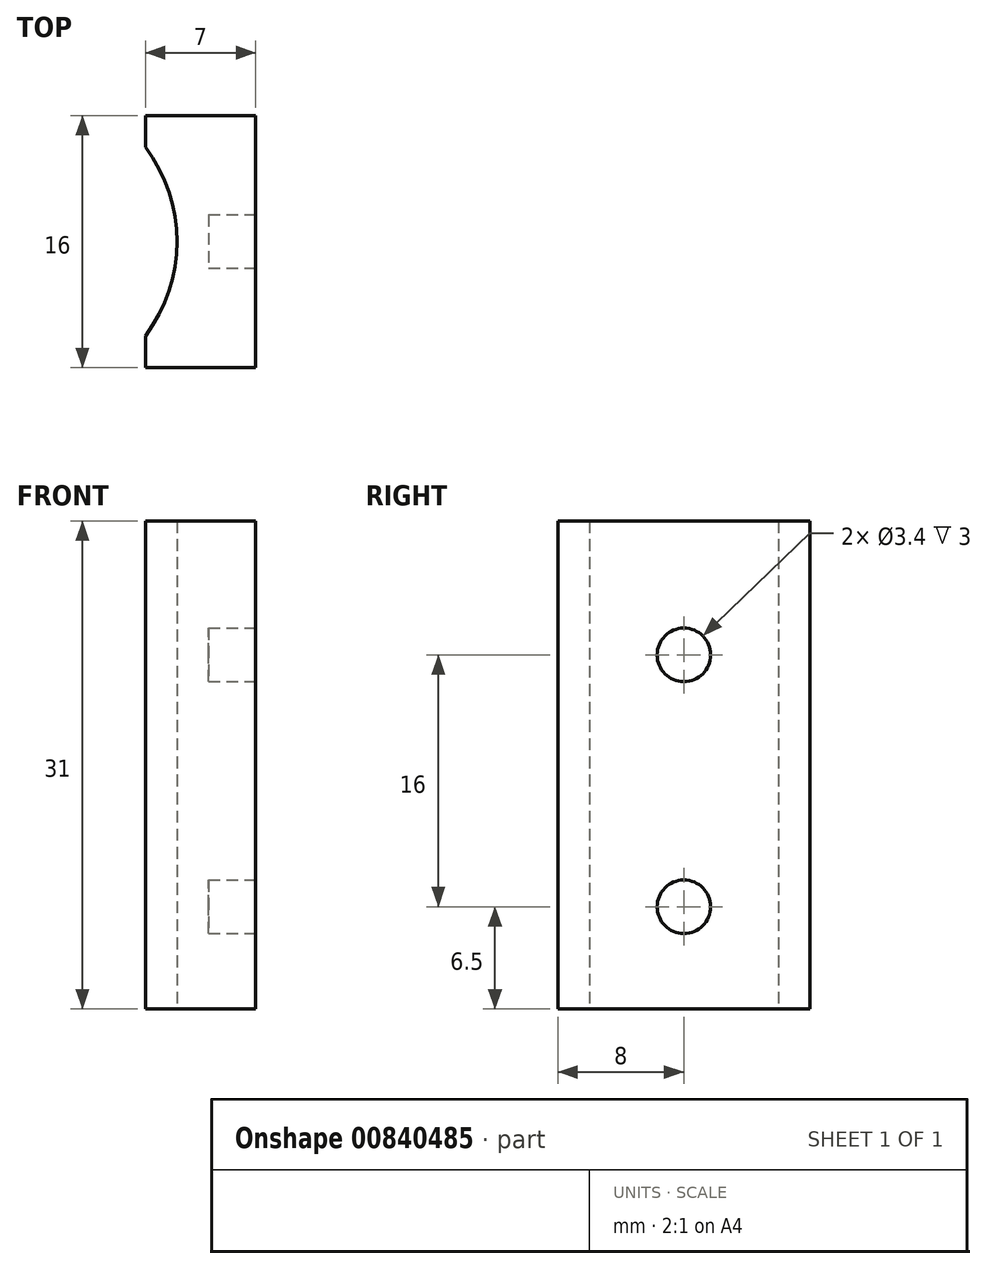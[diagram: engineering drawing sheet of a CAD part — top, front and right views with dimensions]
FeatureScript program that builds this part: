
annotation { "Feature Type Name" : "Feature", "Feature Type Description" : "" }
export const myFeature = defineFeature(function(context is Context, id is Id, definition is map)
    precondition{}
    {
        {
            var Q0;
            Q0=qCreatedBy(makeId("Top.planeOp"),FACE);
            var sketch = newSketch(context, id + "F0", { "sketchPlane" : qUnion([Q0])});
            skPoint(sketch, "E0.0", {"position": v(4.3, 0) * mm});
            skPoint(sketch, "E1.0", {"position": v(-0.7, 0) * mm});
            skLineSegment(sketch, "E2.bottom", {"start": v(-2.7, -8) * mm, "end": v(4.3, -8) * mm});
            skLineSegment(sketch, "E2.top", {"start": v(-2.7, 8) * mm, "end": v(4.3, 8) * mm});
            skLineSegment(sketch, "E2.left", {"start": v(-2.7, -8) * mm, "end": v(-2.7, 8) * mm});
            skLineSegment(sketch, "E2.right", {"start": v(4.3, -8) * mm, "end": v(4.3, 8) * mm});
            skArc(sketch, "E3", {"start": v(-2.7, -6) * mm, "mid": v(-0.7, 0) * mm, "end": v(-2.7, 6) * mm});
            skLineSegment(sketch, "E4", {"start": v(-2.7, 6) * mm, "end": v(-2.7, 6) * mm});
            skLineSegment(sketch, "E5", {"start": v(-2.7, -6) * mm, "end": v(-2.7, -6) * mm});
            skSolve(sketch);
        }
        {
            var Q0;
            {var subQ3=sQuery(id+"F0.wireOp",EDGE,"E2.bottom");Q0=makeQuery(id+"F0.imprint","IMPRINT",FACE,{"disambiguationData":[TD([[makeQuery(id+"F0.imprint","IMPRINT",EDGE,{"derivedFrom":subQ3}),1.0]])]});}
            extrude(context, id + "F1", {"entities" : qUnion([Q0]), "depth" : 31 * mm, "offsetDistance" : 25 * mm});
        }
        {
            var Q0;
            Q0=makeQuery(id+"F1.opExtrude","SWEPT_FACE",FACE,{"disambiguationData":[OSD([sQuery(id+"F0.wireOp",EDGE,"E2.right")])]});
            var sketch = newSketch(context, id + "F2", { "sketchPlane" : qUnion([Q0])});
            skLineSegment(sketch, "E6.0", {"start": v(-8, 31) * mm, "end": v(8, 31) * mm});
            skLineSegment(sketch, "E7.0", {"start": v(-8, 0) * mm, "end": v(8, 0) * mm});
            skCircle(sketch, "E8", {"center": v(0, 22.5) * mm, "radius": 1.7 * mm});
            skCircle(sketch, "E9", {"center": v(0, 6.5) * mm, "radius": 1.7 * mm});
            skSolve(sketch);
        }
        {
            var Q0;
            Q0=makeQuery(id+"F2.imprint","IMPRINT",FACE,{"disambiguationData":[TD([[makeQuery(id+"F2.imprint","IMPRINT",EDGE,{"derivedFrom":sQuery(id+"F2.wireOp",EDGE,"E8")}),1.0]])]});
            var Q1;
            Q1=makeQuery(id+"F2.imprint","IMPRINT",FACE,{"disambiguationData":[TD([[makeQuery(id+"F2.imprint","IMPRINT",EDGE,{"derivedFrom":sQuery(id+"F2.wireOp",EDGE,"E9")}),1.0]])]});
            extrude(context, id + "F3", {"entities" : qUnion([Q0, Q1]), "operationType" : NewBodyOperationType.REMOVE, "oppositeDirection" : true, "depth" : 3 * mm, "offsetDistance" : 25 * mm});
        }
    });
